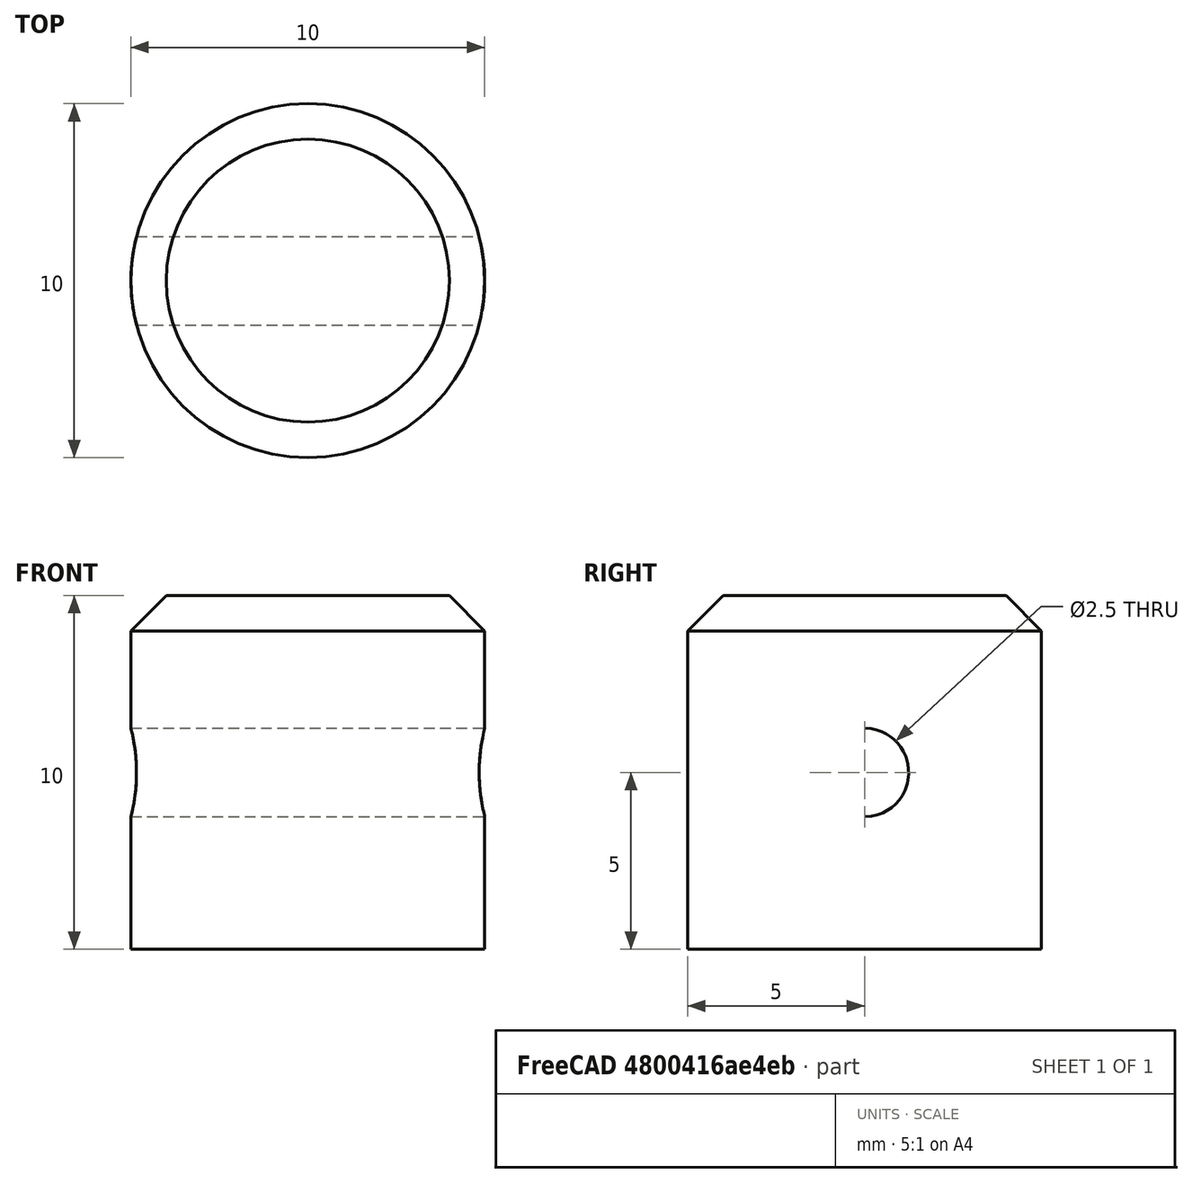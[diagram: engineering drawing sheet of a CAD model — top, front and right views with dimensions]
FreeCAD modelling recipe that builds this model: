
FCSTD DOCUMENT  (FreeCAD 0.14R3702 (Git))
Label: pied
License: CC-BY 3.0
LicenseURL: http://creativecommons.org/licenses/by/3.0/
objects: Part::Part2DObjectPython×6, Part::Feature×6, Part::RuledSurface×4, Part::Cylinder×2, Part::MultiFuse×1, Part::Cut×1, Part::Chamfer×1
note: 21 computed .brp shape members not serialized (recipe doc carries the construction recipe); baked Part::Feature solids carry a one-line shape summary decoded from their .brp

FEATURE [Part::Part2DObjectPython] Line  # Draft 2D object (typed FeaturePython)
  ChamferSize = 0
  Closed = false
  End = (7.5,7.5,0)
  FilletRadius = 0
  MakeFace = false
  Points = (2) [(-7.5,-7.5,0),(7.5,7.5,0)]
  Start = (-7.5,-7.5,0)
FEATURE [Part::Part2DObjectPython] Line001  # Draft 2D object (typed FeaturePython)
  ChamferSize = 0
  Closed = false
  End = (-7.5,7.5,0)
  FilletRadius = 0
  MakeFace = false
  Points = (2) [(7.5,-7.5,0),(-7.5,7.5,0)]
  Start = (7.5,-7.5,0)
FEATURE [Part::Part2DObjectPython] Circle  # Draft 2D object (typed FeaturePython)
  FirstAngle = 45
  LastAngle = 135
  MakeFace = false
  Radius = 5
FEATURE [Part::Feature] Edge
  Placement = pos=(-7.5,-7.5,2) rot=(0,0,1;0rad)
  shape: bbox 2e-07 x 15 x 2e-07 mm, 0 faces, 0 solids (baked)
FEATURE [Part::Feature] Edge001
  Placement = pos=(-7.5,-7.5,2) rot=(0,0,1;0rad)
  shape: bbox 15 x 2e-07 x 2e-07 mm, 0 faces, 0 solids (baked)
FEATURE [Part::Feature] Edge002
  Placement = pos=(-7.5,-7.5,2) rot=(0,0,1;0rad)
  shape: bbox 2e-07 x 15 x 2e-07 mm, 0 faces, 0 solids (baked)
FEATURE [Part::Feature] Edge003
  Placement = pos=(-7.5,-7.5,2) rot=(0,0,1;0rad)
  shape: bbox 15 x 2e-07 x 2e-07 mm, 0 faces, 0 solids (baked)
FEATURE [Part::Part2DObjectPython] Circle001  # Draft 2D object (typed FeaturePython)
  FirstAngle = 225
  LastAngle = 315
  MakeFace = false
  Radius = 5
FEATURE [Part::Part2DObjectPython] Circle002  # Draft 2D object (typed FeaturePython)
  FirstAngle = 135
  LastAngle = 225
  MakeFace = false
  Radius = 5
FEATURE [Part::Part2DObjectPython] Circle003  # Draft 2D object (typed FeaturePython)
  FirstAngle = 315
  LastAngle = 45
  MakeFace = false
  Radius = 5
FEATURE [Part::RuledSurface] Ruled_Surface
  Curve1 = -> Edge
  Curve2 = -> Circle002
  Orientation = 0
FEATURE [Part::RuledSurface] Ruled_Surface001
  Curve1 = -> Edge001 [Edge1]
  Curve2 = -> Circle [Edge1]
  Orientation = 0
FEATURE [Part::RuledSurface] Ruled_Surface002
  Curve1 = -> Edge002 [Edge1]
  Curve2 = -> Circle003 [Edge1]
  Orientation = 0
FEATURE [Part::RuledSurface] Ruled_Surface003
  Curve1 = -> Circle001 [Edge1]
  Curve2 = -> Edge003 [Edge1]
  Orientation = 0
FEATURE [Part::Feature] Face
  shape: bbox 10 x 10 x 2e-07 mm, 1 faces, 0 solids (baked)
FEATURE [Part::Feature] Face001
  Placement = pos=(0,0,2) rot=(0,0,1;0rad)
  shape: bbox 15 x 15 x 2e-07 mm, 1 faces, 0 solids (baked)
FEATURE [Part::Cylinder] Cylinder  label="insert"
  Angle = 360
  Height = 10
  Placement = pos=(0,0,2) rot=(0,0,1;0rad)
  Radius = 5
FEATURE [Part::Cylinder] Cylinder001  label="Cylindre001"
  Angle = 360
  Height = 10
  Placement = pos=(-5,0,7) rot=(0,1,0;1.5708rad)
  Radius = 1.25
FEATURE [Part::MultiFuse] Fusion  label="patin"
  Shapes = -> [Ruled_Surface,Ruled_Surface001,Ruled_Surface002,Ruled_Surface003,Face,Face001]
FEATURE [Part::Cut] Cut
  Base = -> Cylinder
  Tool = -> Cylinder001
FEATURE [Part::Chamfer] Chamfer
  Base = -> Cut
  Edges = 1 edges r=1: [Edge6]
